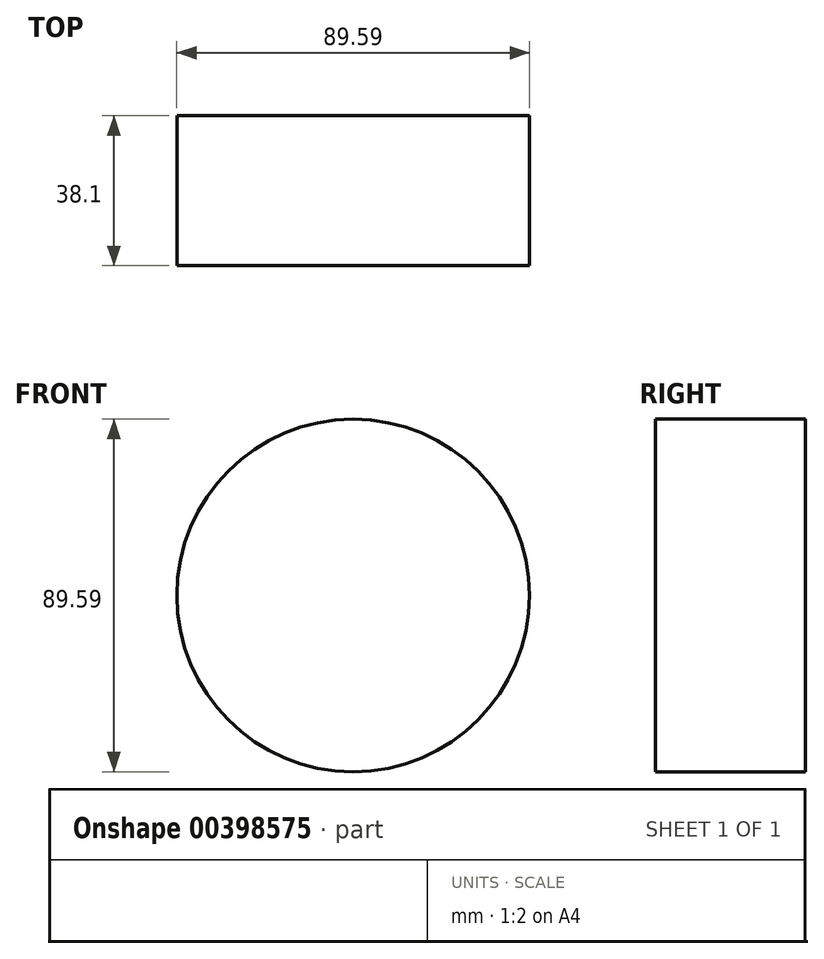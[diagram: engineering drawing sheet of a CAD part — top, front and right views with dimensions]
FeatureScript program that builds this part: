
annotation { "Feature Type Name" : "Feature", "Feature Type Description" : "" }
export const myFeature = defineFeature(function(context is Context, id is Id, definition is map)
    precondition{}
    {
        {
            var Q0;
            Q0=qCreatedBy(makeId("Front.planeOp"),FACE);
            var sketch = newSketch(context, id + "F0", { "sketchPlane" : qUnion([Q0])});
            skCircle(sketch, "E0", {"center": v(23.62, 54.05) * mm, "radius": 44.8 * mm});
            skSolve(sketch);
        }
        {
            var Q0;
            Q0=makeQuery(id+"F0.imprint","IMPRINT",FACE,{"disambiguationData":[TD([[makeQuery(id+"F0.imprint","IMPRINT",EDGE,{"derivedFrom":sQuery(id+"F0.wireOp",EDGE,"E0")}),1.0]])]});
            var Q1;
            Q1=sQuery(id+"F0.wireOp",EDGE,"E0");
            extrude(context, id + "F1", {"entities" : qUnion([Q0]), "surfaceEntities" : qUnion([Q1]), "depth" : 38.1 * mm});
        }
    });
